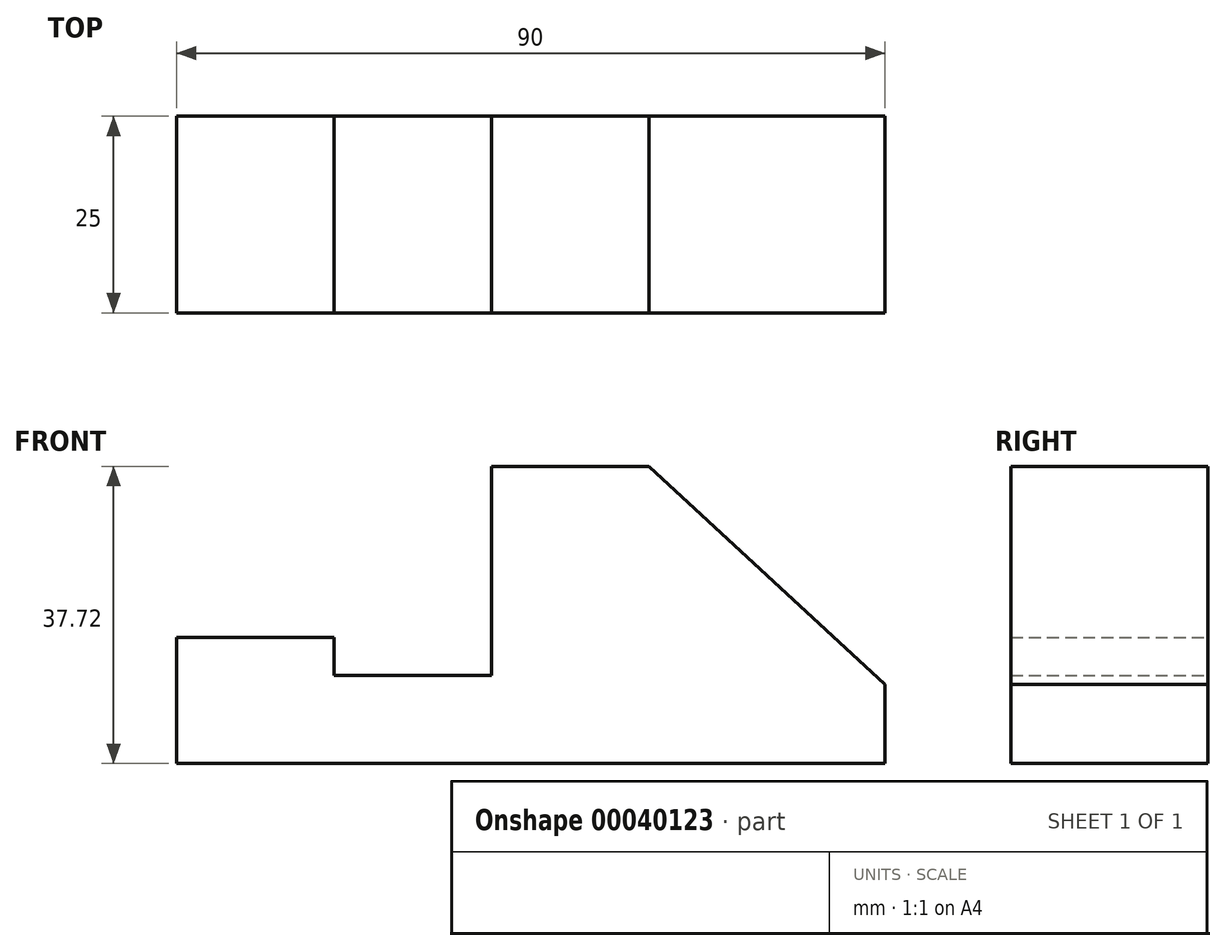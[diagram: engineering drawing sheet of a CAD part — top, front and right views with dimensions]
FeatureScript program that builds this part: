
annotation { "Feature Type Name" : "Feature", "Feature Type Description" : "" }
export const myFeature = defineFeature(function(context is Context, id is Id, definition is map)
    precondition{}
    {
        {
            var Q0;
            Q0=qCreatedBy(makeId("Front.planeOp"),FACE);
            var sketch = newSketch(context, id + "F0", { "sketchPlane" : qUnion([Q0])});
            skLineSegment(sketch, "E0", {"start": v(-40, 21.57) * mm, "end": v(-40, 5.57) * mm});
            skLineSegment(sketch, "E1", {"start": v(-40, 5.57) * mm, "end": v(50, 5.57) * mm});
            skLineSegment(sketch, "E2", {"start": v(50, 5.57) * mm, "end": v(50, 15.57) * mm});
            skLineSegment(sketch, "E3", {"start": v(50, 15.57) * mm, "end": v(20, 43.29) * mm});
            skLineSegment(sketch, "E4", {"start": v(20, 43.29) * mm, "end": v(0, 43.29) * mm});
            skLineSegment(sketch, "E5", {"start": v(0, 43.29) * mm, "end": v(0, 16.71) * mm});
            skLineSegment(sketch, "E6", {"start": v(0, 16.71) * mm, "end": v(-20, 16.71) * mm});
            skLineSegment(sketch, "E7", {"start": v(-20, 16.71) * mm, "end": v(-20, 21.57) * mm});
            skLineSegment(sketch, "E8", {"start": v(-20, 21.57) * mm, "end": v(-40, 21.57) * mm});
            skSolve(sketch);
        }
        {
            var Q0;
            Q0 = qSketchRegion(id + "F0", true);
            extrude(context, id + "F1", {"entities" : qUnion([Q0]), "depth" : 25 * mm});
        }
    });
